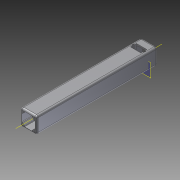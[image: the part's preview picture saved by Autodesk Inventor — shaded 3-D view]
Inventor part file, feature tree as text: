
AUTODESK INVENTOR PART (.ipt)
format: ipt  version: 2012 (Build 160160000, 160)  size: 317,440 bytes
history: native  units: in
note: dims shown in document units (in); Inventor stores cm internally (conversion verified against a paired STEP export)
features: extrude x9, sketch x9, projected_geometry x4, fillet x2, other x2, plane x1, reference x1
ambient origin geometry x8: Origin, YZ Plane, XZ Plane, XY Plane, X Axis, Y Axis, Z Axis, Center Point
bodies: Solid1 (feature_tree)
feature tree (28):
  extrude  "Extrusion1"  TaperAngle=135.0deg  [1 undecoded]
  sketch  "Sketch8"  dims[d37=45.0deg d39=0.03in d44=7.874in d45=0.0in d65=0.4331in]
  plane  "Work Plane1"
  extrude  "Extrusion9"  Depth=0.03in
  fillet  "Fillet1"  Radius=7.874in
  fillet  "Fillet2"  Radius=0.4331in
  extrude  "Extrusion14"  Depth=0.2504in
  extrude  "Extrusion15"  Depth=0.0394in
  extrude  "Extrusion16"  Depth=0.0984in
  extrude  "Extrusion17"  Depth=0.0984in
  extrude  "Extrusion18"  Depth=0.1181in
  extrude  "Extrusion19"  Depth=0.3937in TaperAngle=0.0deg
  extrude  "Extrusion20"  Depth=0.3937in TaperAngle=0.0deg
  other  "Work Axis1"
  other  "Work Axis2"
  sketch  "Sketch2"  dims[d21=0.015in d28=135.0deg]
  sketch  "Sketch13"  dims[d66=0.4331in d72=0.2504in]
  sketch  "Sketch14"  dims[d73=0.1969in d74=0.0394in]
  reference  "Reference10"
  sketch  "Sketch15"  dims[d79=0.0984in d80=0.0984in]
  sketch  "Sketch16"  dims[d81=0.0984in d82=0.0984in]
  sketch  "Sketch17"  dims[d85=0.3937in d86=0.0in d97=0.1181in]
  projected_geometry  "Projected Loop3"
  projected_geometry  "Projected Loop4"
  projected_geometry  "Projected Loop5"
  projected_geometry  "Projected Loop6"
  sketch  "Sketch18"  dims[d98=0.1181in d103=0.3937in d104=0.0in]
  sketch  "Sketch19"  dims[d106=0.0118in d107=0.3937in d108=0.0in d109=0.3937in d110=0.0in d111=0.3937in d112=0.1312in d113=0.1312in d114=0.0591in d115=0.0591in d116=0.1312in d117=0.1312in d118=0.3937in d119=0.0in d120=0.3937in d121=0.0in d122=0.3937in d123=0.0in d124=0.1969in d125=0.0in]
note: 1 required parameter value undecoded (feature->parameter linkage not recoverable at this tier; creation-order binding heuristic only, values carry confidence <= 0.55)
